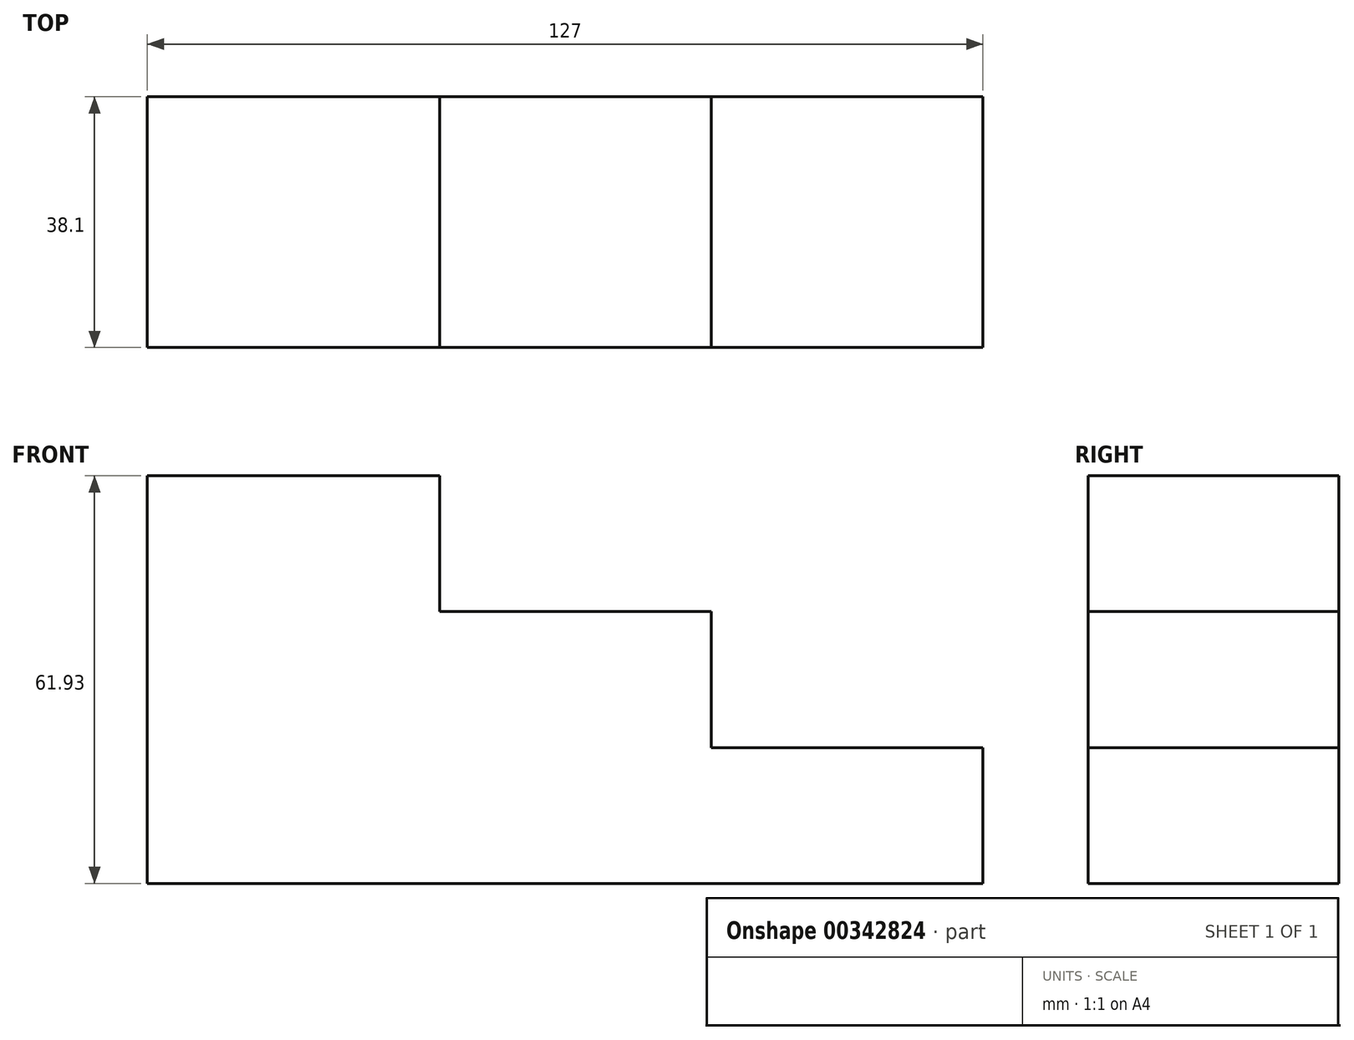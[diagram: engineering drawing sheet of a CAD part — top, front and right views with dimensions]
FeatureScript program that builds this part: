
annotation { "Feature Type Name" : "Feature", "Feature Type Description" : "" }
export const myFeature = defineFeature(function(context is Context, id is Id, definition is map)
    precondition{}
    {
        {
            var Q0;
            Q0=qCreatedBy(makeId("Front.planeOp"),FACE);
            var sketch = newSketch(context, id + "F0", { "sketchPlane" : qUnion([Q0])});
            skLineSegment(sketch, "E0", {"start": v(-57.84, -40.8) * mm, "end": v(69.16, -40.8) * mm});
            skLineSegment(sketch, "E1", {"start": v(69.16, -40.8) * mm, "end": v(69.16, -20.17) * mm});
            skLineSegment(sketch, "E2", {"start": v(69.16, -20.17) * mm, "end": v(27.89, -20.17) * mm});
            skLineSegment(sketch, "E3", {"start": v(27.89, -20.17) * mm, "end": v(27.89, 0.48) * mm});
            skLineSegment(sketch, "E4", {"start": v(27.89, 0.48) * mm, "end": v(-13.39, 0.48) * mm});
            skLineSegment(sketch, "E5", {"start": v(-13.39, 0.48) * mm, "end": v(-13.39, 21.13) * mm});
            skLineSegment(sketch, "E6", {"start": v(-13.39, 21.13) * mm, "end": v(-57.84, 21.13) * mm});
            skLineSegment(sketch, "E7", {"start": v(-57.84, 21.13) * mm, "end": v(-57.84, -40.8) * mm});
            skSolve(sketch);
        }
        {
            var Q0;
            Q0=makeQuery(id+"F0.imprint","IMPRINT",FACE,{"disambiguationData":[TD([[makeQuery(id+"F0.imprint","IMPRINT",EDGE,{"derivedFrom":sQuery(id+"F0.wireOp",EDGE,"E0")}),1.0]])]});
            extrude(context, id + "F1", {"entities" : qUnion([Q0]), "depth" : 38.1 * mm});
        }
    });
